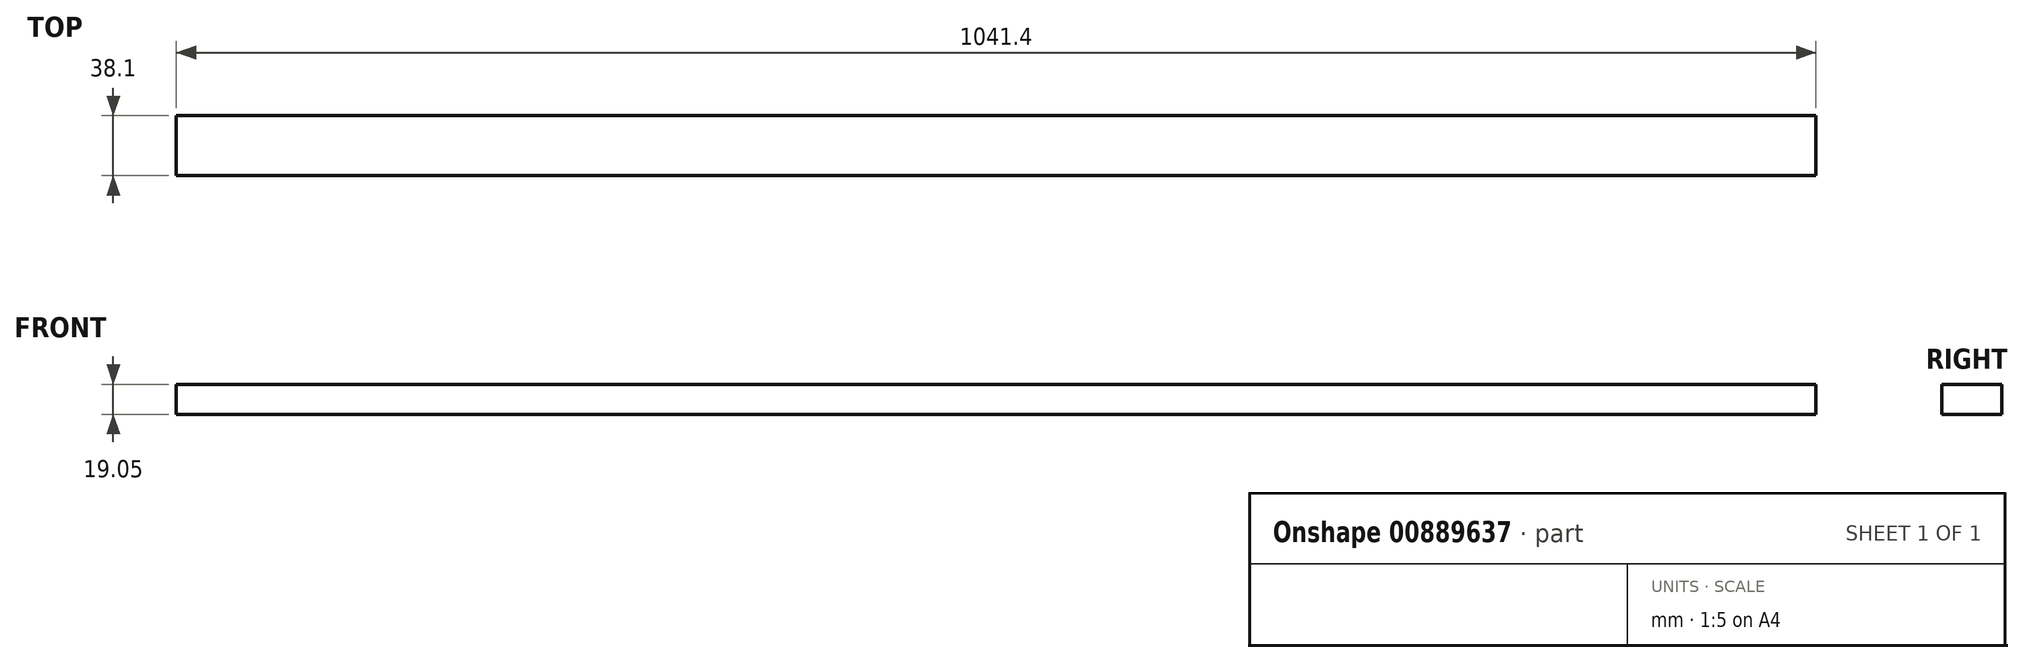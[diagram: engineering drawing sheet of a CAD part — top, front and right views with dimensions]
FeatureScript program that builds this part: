
annotation { "Feature Type Name" : "Feature", "Feature Type Description" : "" }
export const myFeature = defineFeature(function(context is Context, id is Id, definition is map)
    precondition{}
    {
        {
            var Q0;
            Q0=qCreatedBy(makeId("Top.planeOp"),FACE);
            var sketch = newSketch(context, id + "F0", { "sketchPlane" : qUnion([Q0])});
            skLineSegment(sketch, "E0.bottom", {"start": v(0, 0) * mm, "end": v(1041.4, 0) * mm});
            skLineSegment(sketch, "E0.top", {"start": v(0, 38.1) * mm, "end": v(1041.4, 38.1) * mm});
            skLineSegment(sketch, "E0.left", {"start": v(0, 0) * mm, "end": v(0, 38.1) * mm});
            skLineSegment(sketch, "E0.right", {"start": v(1041.4, 0) * mm, "end": v(1041.4, 38.1) * mm});
            skSolve(sketch);
        }
        {
            var Q0;
            Q0 = qSketchRegion(id + "F0", true);
            extrude(context, id + "F1", {"entities" : qUnion([Q0]), "depth" : 19.05 * mm, "offsetDistance" : 25.4 * mm});
        }
    });
